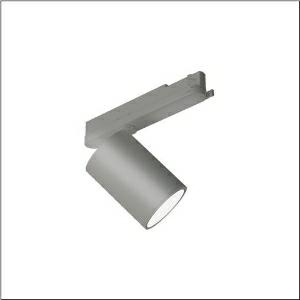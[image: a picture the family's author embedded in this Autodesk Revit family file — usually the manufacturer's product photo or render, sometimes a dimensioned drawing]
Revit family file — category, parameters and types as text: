
# Revit family: spot_31_51sf63mab4b
name_source: partatom
category: Lighting Fixtures
units: mm (PartAtom-declared; Revit-internal decimal feet)

## family parameters
Cut with Voids When Loaded = No
Host = Face
Light Source = No
Part Type = Normal
Room Calculation Point = No
Round Connector Dimension = Use Diameter
Shared = No

## types (1)
- --- (1 x LED, 5030 lm, 41.7 W, 3000K)
    Apparent Load = 42 VA
    CIE Flux Codes = 92 97 99 100 100
    Color Rendering = 90
    Color Temperature = 3000K
    Default Elevation = 1800 mm
    Description = Spot 31, directional spotlight, light control with lens, of PMMA, LED rated luminous flux: 4.830lm, light colour: 930, with 3-phase adapter, mains connection: 220..240V, AC, 50/60Hz, of aluminium, metallic grey (RAL 9006), length: 213mm, diameter: 90mm, protection rating (complete): IP20, insulation class (complete): insulation class I (protective earthing), certification: CE, impact resistance: IK02, permissible ambient temperature for indoor applications: -20..+40°C, packaging unit: 1 piece
    Height = 175 mm
    Lamp = 1 x LED
    Lamp Light Flux = 5030 lm
    Lamp Power = 41.7 W
    Lamp count = 1
    Length = 90 mm
    Luminous efficacy = 121 lm/W
    Manufacturer = Siteco
    ModVariant = No
    Model = 51SF63MAB4B
    Mounting Place = Ceiling
    Mounting Type = Pendant
    Number of Poles = 1
    OnlyDefault = Yes
    Power Factor = 1
    Product Name = Spot 31
    Product group = directional spotlight
    ProductGroupID = 905
    Protection Class = Protection class I
    Protection Degree = IP 20
    RLX_Detail_Level = 1
    RLX_Emergency_Light_Flux = 0 lm
    RLX_Emergency_Type = 0
    RLX_Emergency_Type_DB = No
    RlxData = <blob elided: 19981 chars, md5=592f67a8>
    Socket = socket
    Standby Power = 0 W
    System Light Flux = 5030 lm
    System Power = 42 W
    Type Comments = factory setting: luminous flux: 100 % | (ON | ON | ON | ON) | 1050 mA
    Type Image = l_1273725.jpg
    URL = http://relux.com
    VarID = @adj_167817
    Voltage = 0 V
    Weight = 0.00 kg
    Width = 0 mm  [stored 0 ft]

note: [stored X ft] marks values corroborated as IEEE doubles in the binary element streams (Revit-internal decimal feet)

## geometry (parser evidence)
native form markers: Blend x4, Sweep x9
no freeform markers — native parametric forms only
